# Revit family: Specialty-Equipment_Shield Casework_Headwall-With-Canopy-1
name_source: partatom
category: Specialty Equipment
units: mm (PartAtom-declared; Revit-internal decimal feet)

## family parameters
Always vertical = Yes
Cut with Voids When Loaded = No
OmniClass Number = 23.40.35.17.34
OmniClass Title = Medical Casework
Part Type = Normal
Room Calculation Point = No
Round Connector Dimension = Use Diameter
Shared = No
Work Plane-Based = No

## types (1)
- Not a Type - Please Load Type Catalog
    Assembly Code = E1020810
    Ceiling Height = 96 "
    Default Elevation = 0 "
    Description = Headwall With Canopy
    Edition number = 1
    Headwall Width = 84 "
    Keynote = 11700
    Manufacturer = Shield Casework
    Model = Headwall With Canopy
    Product Guid = 069aae4b-69cd-4fe3-b77a-b1e21477a868
    Product data url = https://www.bimobject.com
    Product url = https://shieldheadwalls.com
    URL = https://www.shieldcasework.com
    |CSegHgh = 45.05 "
    |CSegWdt = 24.44 "
    |LRSegOOff = 38.96 "
    |Sub0810 = No
    |TSegOOff = 66 "

## geometry (parser evidence)
native form markers: Sweep x13
no freeform markers — native parametric forms only
